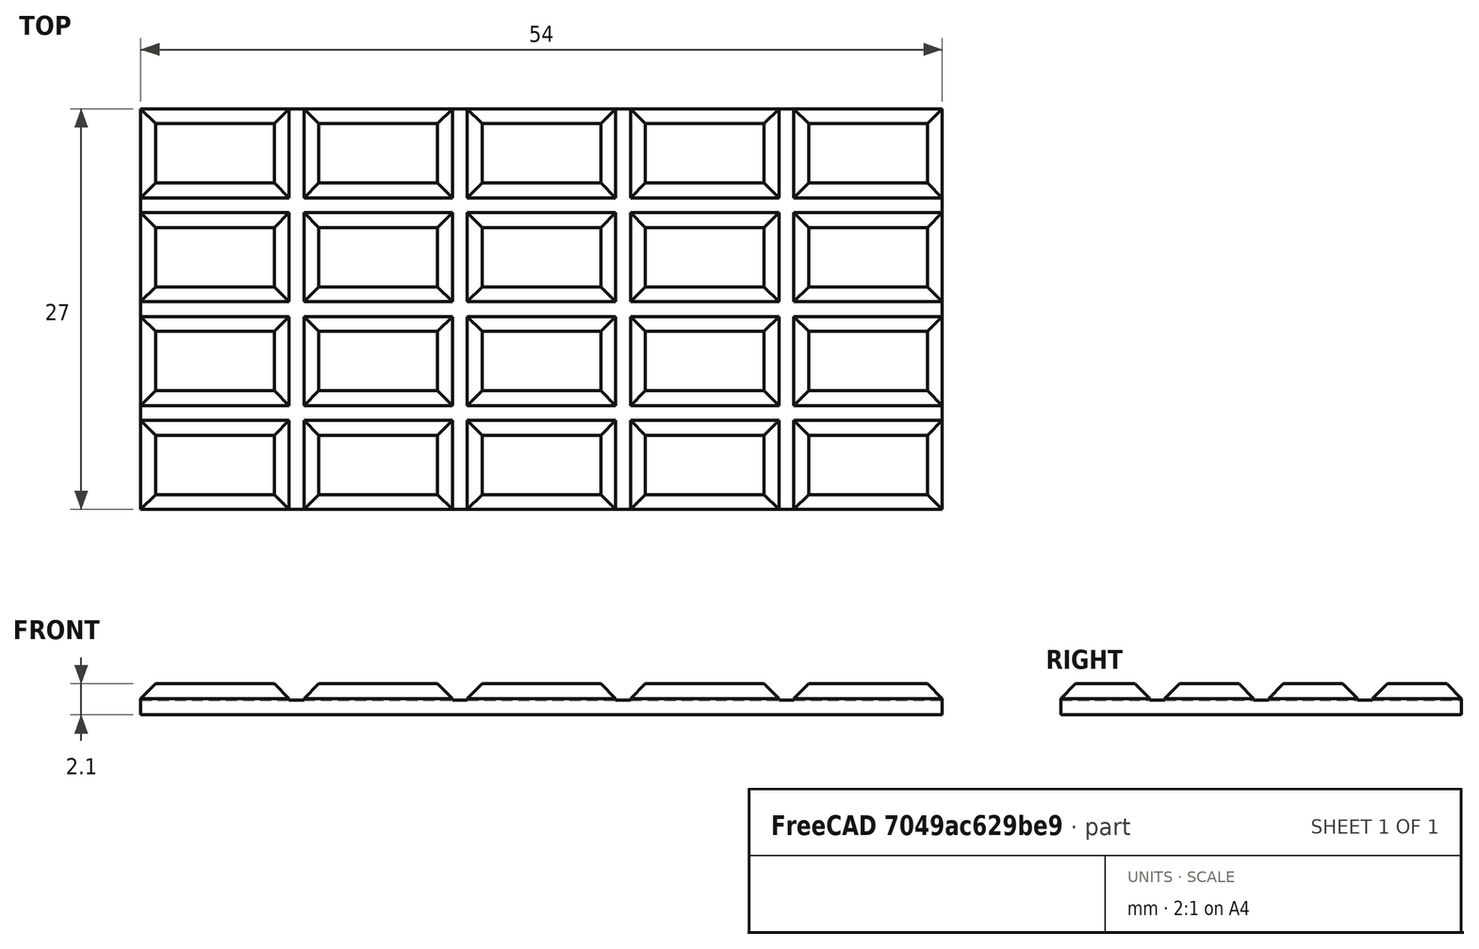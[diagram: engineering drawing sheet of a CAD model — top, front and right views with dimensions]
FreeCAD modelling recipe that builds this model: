
FCSTD DOCUMENT  (FreeCAD 0.16R6707 (Git))
Label: Tableta_choco
License: CreativeCommons Attribution-ShareAlike
LicenseURL: http://creativecommons.org/licenses/by-sa/4.0/
objects: Part::Box×2, Part::Chamfer×1, Part::FeaturePython×1, Part::MultiFuse×1
note: 5 computed .brp shape members not serialized (recipe doc carries the construction recipe); baked Part::Feature solids carry a one-line shape summary decoded from their .brp

FEATURE [Part::Box] Box  label="Base"
  Height = 1
  Length = 54
  Width = 27
FEATURE [Part::Box] Box001  label="base_onza"
  Height = 1.1
  Length = 10
  Placement = pos=(0,0,1) rot=(0,0,1;0rad)
  Width = 6
FEATURE [Part::Chamfer] Chamfer  label="onza"
  Base = -> Box001
  Edges = 4 edges r=1: [Edge2,Edge6,Edge10,Edge12]
FEATURE [Part::FeaturePython] Array  # Draft array (typed FeaturePython)
  Angle = 360
  ArrayType = 0
  Axis = (0,0,1)
  Base = -> Chamfer
  Center = (0,0,0)
  Fuse = false
  IntervalAxis = (0,0,0)
  IntervalX = (11,0,0)
  IntervalY = (0,7,0)
  IntervalZ = (0,0,0)
  NumberPolar = 1
  NumberX = 5
  NumberY = 4
  NumberZ = 1
FEATURE [Part::MultiFuse] Fusion  label="Tableta"
  Shapes = -> [Box,Array]
